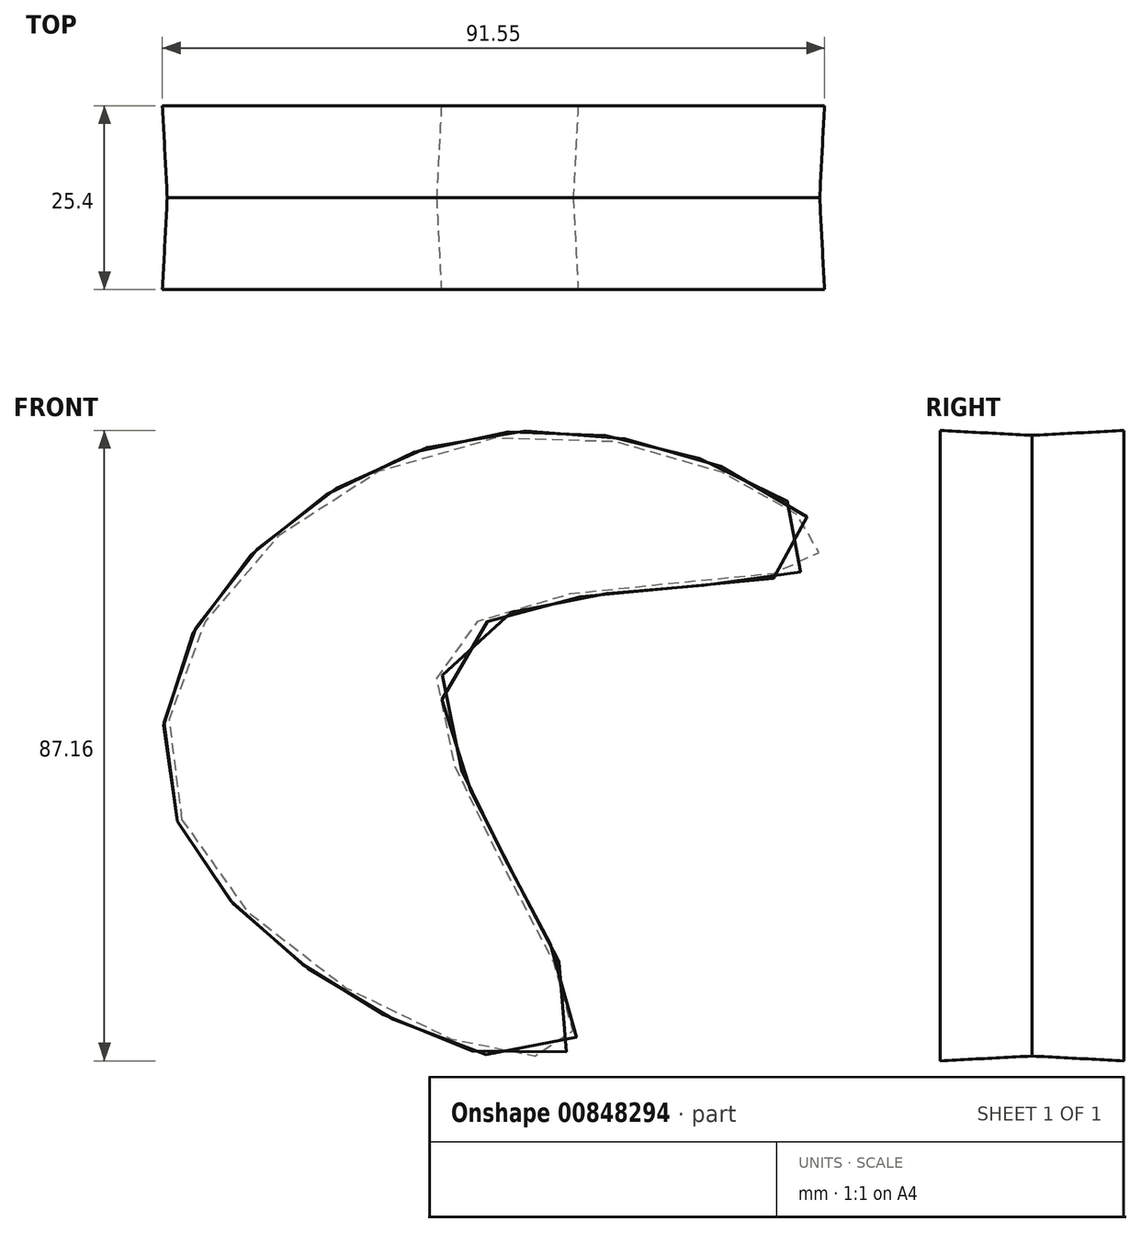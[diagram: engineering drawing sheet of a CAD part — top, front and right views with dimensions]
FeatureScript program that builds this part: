
annotation { "Feature Type Name" : "Feature", "Feature Type Description" : "" }
export const myFeature = defineFeature(function(context is Context, id is Id, definition is map)
    precondition{}
    {
        {
            var Q0;
            Q0=qCreatedBy(makeId("Front.planeOp"),FACE);
            var sketch = newSketch(context, id + "F0", { "sketchPlane" : qUnion([Q0])});
            skFitSpline(sketch, "E0", {"points": [v(-17.45, 22.87) * mm, v(33.88, 36.08) * mm, v(-9.32, 52.85) * mm, v(-53.7, 0) * mm, v(0, -30.49) * mm, v(-17.45, 22.87) * mm]});
            skSolve(sketch);
        }
        {
            var Q0;
            Q0=makeQuery(id+"F0.imprint","IMPRINT",FACE,{"disambiguationData":[TD([[makeQuery(id+"F0.imprint","IMPRINT",EDGE,{"derivedFrom":sQuery(id+"F0.wireOp",EDGE,"E0")}),1.0]])]});
            extrude(context, id + "F1", {"entities" : qUnion([Q0]), "endBound" : BoundingType.SYMMETRIC, "depth" : 25.4 * mm, "offsetDistance" : 25.4 * mm, "hasDraft" : true, "draftAngle" : 3 * degree});
        }
    });
